# Revit family: isFang-Fangmast
name_source: partatom
category: Generic Models
revit_build: Autodesk Revit 2015 (Build: 20140606_1530(x64)
units: mm (PartAtom-declared; Revit-internal decimal feet)

## types (9) — shared parameters
Height 1 = 1000 mm  [stored 3.28084 ft]
Height 2 = 1000 mm  [stored 3.28084 ft]
Manufacturer = OBO Bettermann
Material = Aluminum
URL = http://www.obo-bettermann.com

## per-type parameters (varying)
| type | GTIN | Height | Manufacturer Art.No. |
| 101 3B-4000 | 4012195674733 | 2000 mm  [stored 6.56168 ft] | 5402864 |
| 101 3B-4500 | 4012195674740 | 2500 mm  [stored 8.2021 ft] | 5402866 |
| 101 3B-5000 | 4012195674757 | 3000 mm  [stored 9.84252 ft] | 5402868 |
| 101 3B-5500 | 4012195674764 | 3500 mm  [stored 11.4829 ft] | 5402870 |
| 101 3B-6000 | 4012195674795 | 4000 mm  [stored 13.1234 ft] | 5402872 |
| 101 3B-6500 | 4012195674801 | 4500 mm | 5402874 |
| 101 3B-7000 | 4012195674818 | 5000 mm  [stored 16.4042 ft] | 5402876 |
| 101 3B-7500 | 4012195674825 | 5500 mm  [stored 18.0446 ft] | 5402878 |
| 101 3B-8000 | 4012195674856 | 6000 mm  [stored 19.685 ft] | 5402880 |

note: column(s) folded — value = type name in every type: Article Type

note: [stored X ft] marks values corroborated as IEEE doubles in the binary element streams (Revit-internal decimal feet)

## geometry (parser evidence)
native form markers: Sweep x3
no freeform markers — native parametric forms only
